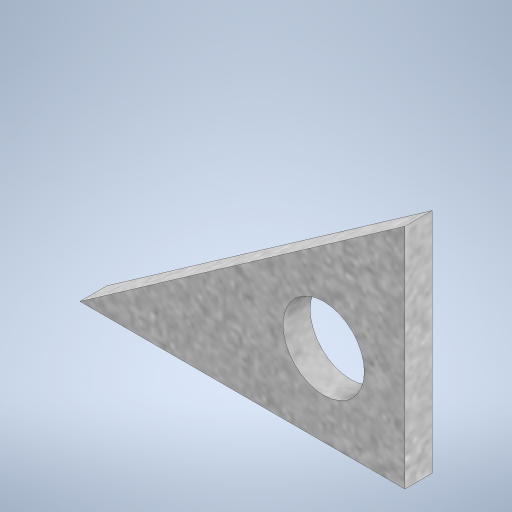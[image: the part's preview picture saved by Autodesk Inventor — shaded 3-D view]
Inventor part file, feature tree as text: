
AUTODESK INVENTOR PART (.ipt)
format: ipt  version: 2024 (Build 280153000, 153)  size: 367,104 bytes
history: native  units: in
note: dims shown in document units (in); Inventor stores cm internally (conversion verified against a paired STEP export)
features: extrude x1, other x1
ambient origin geometry x8: Origin, YZ Plane, XZ Plane, XY Plane, X Axis, Y Axis, Z Axis, Center Point
bodies: Solid1 (feature_tree)
feature tree (2):
  extrude  "triangle extrusion"  Depth=2.1006in
  other  "triangle"
